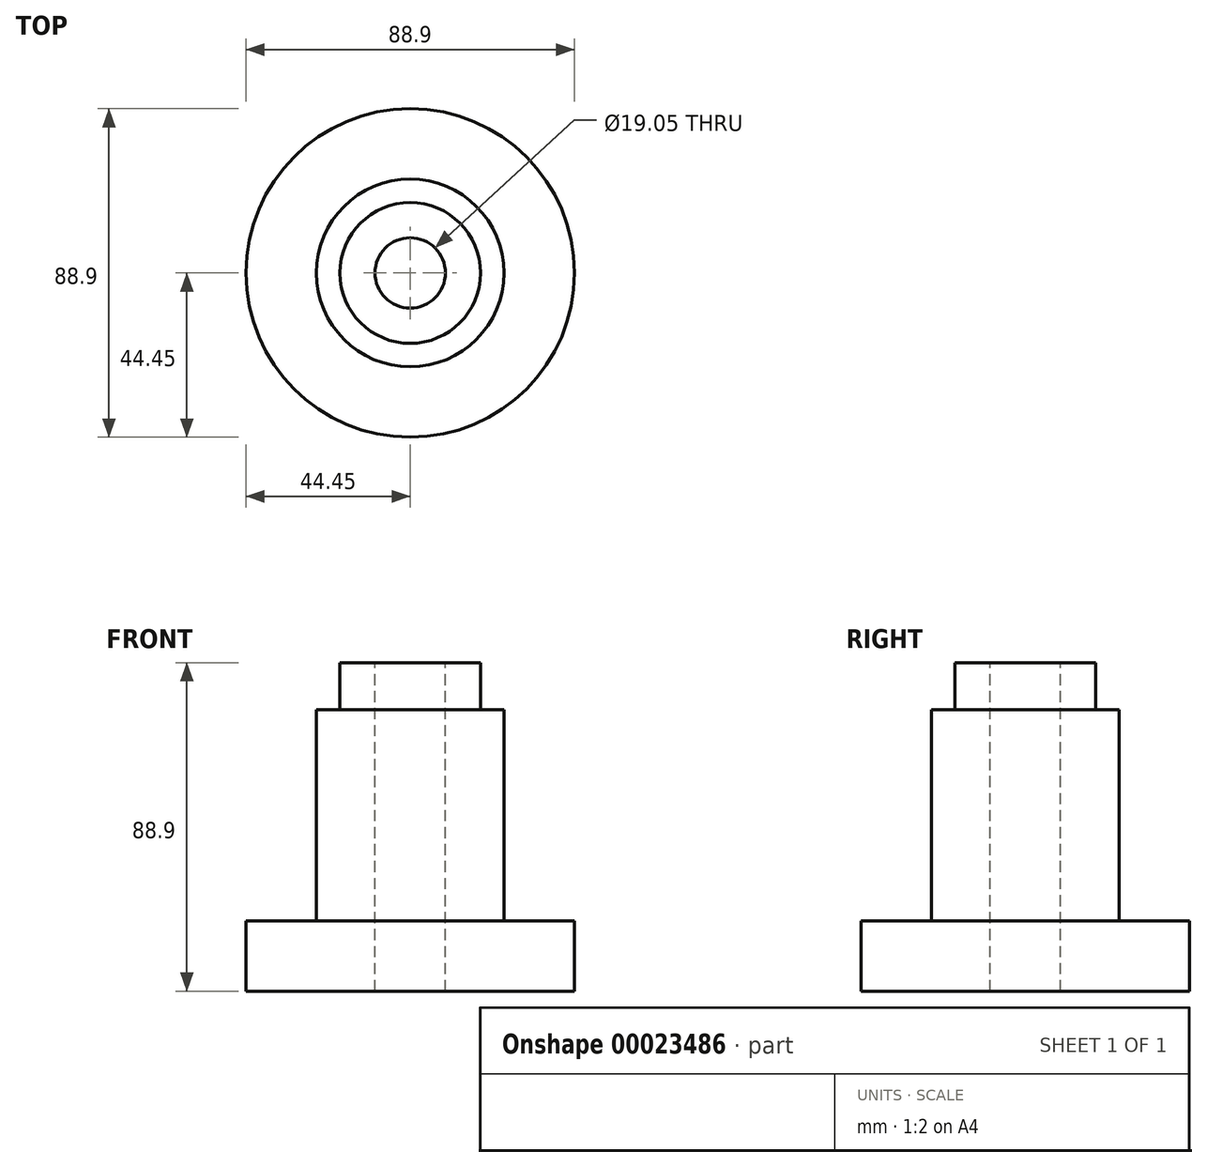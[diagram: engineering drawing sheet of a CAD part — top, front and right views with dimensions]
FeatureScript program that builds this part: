
annotation { "Feature Type Name" : "Feature", "Feature Type Description" : "" }
export const myFeature = defineFeature(function(context is Context, id is Id, definition is map)
    precondition{}
    {
        {
            var Q0;
            Q0=qCreatedBy(makeId("Front.planeOp"),FACE);
            var sketch = newSketch(context, id + "F0", { "sketchPlane" : qUnion([Q0])});
            skLineSegment(sketch, "E0", {"start": v(0, 72.23) * mm, "end": v(0, -76.68) * mm, "construction": true});
            skLineSegment(sketch, "E1.bottom", {"start": v(9.53, 29.69) * mm, "end": v(19.05, 29.69) * mm});
            skLineSegment(sketch, "E1.top", {"start": v(9.53, 16.99) * mm, "end": v(19.05, 16.99) * mm});
            skLineSegment(sketch, "E1.left", {"start": v(9.53, 29.69) * mm, "end": v(9.53, 16.99) * mm});
            skLineSegment(sketch, "E1.right", {"start": v(19.05, 29.69) * mm, "end": v(19.05, 16.99) * mm});
            skLineSegment(sketch, "E2.bottom", {"start": v(9.53, 16.99) * mm, "end": v(25.4, 16.99) * mm});
            skLineSegment(sketch, "E2.top", {"start": v(9.52, -40.16) * mm, "end": v(25.4, -40.16) * mm});
            skLineSegment(sketch, "E2.left", {"start": v(9.53, 16.99) * mm, "end": v(9.53, -40.16) * mm});
            skLineSegment(sketch, "E2.right", {"start": v(25.4, 16.99) * mm, "end": v(25.4, -40.16) * mm});
            skLineSegment(sketch, "E3.bottom", {"start": v(9.52, -40.16) * mm, "end": v(44.45, -40.16) * mm});
            skLineSegment(sketch, "E3.top", {"start": v(9.52, -59.21) * mm, "end": v(44.45, -59.21) * mm});
            skLineSegment(sketch, "E3.left", {"start": v(9.53, -40.16) * mm, "end": v(9.53, -59.21) * mm});
            skLineSegment(sketch, "E3.right", {"start": v(44.45, -40.16) * mm, "end": v(44.45, -59.21) * mm});
            skSolve(sketch);
        }
        {
            var Q0;
            Q0=makeQuery(id+"F0.imprint","IMPRINT",FACE,{"disambiguationData":[TD([[makeQuery(id+"F0.imprint","IMPRINT",EDGE,{"derivedFrom":sQuery(id+"F0.wireOp",EDGE,"E1.bottom")}),-1.0]])]});
            var Q1;
            {var subQ2=sQuery(id+"F0.wireOp",EDGE,"E2.left");Q1=makeQuery(id+"F0.imprint","IMPRINT",FACE,{"disambiguationData":[TD([[makeQuery(id+"F0.imprint","IMPRINT",EDGE,{"derivedFrom":subQ2}),1.0]])]});}
            var Q2;
            Q2=makeQuery(id+"F0.imprint","IMPRINT",FACE,{"disambiguationData":[TD([[makeQuery(id+"F0.imprint","IMPRINT",EDGE,{"derivedFrom":sQuery(id+"F0.wireOp",EDGE,"E3.top")}),1.0]])]});
            var Q3;
            Q3=sQuery(id+"F0.wireOp",EDGE,"E0");
            revolve(context, id + "F1", {"entities" : qUnion([Q0, Q1, Q2]), "axis" : qUnion([Q3]), "revolveType" : RevolveType.FULL});
        }
    });
